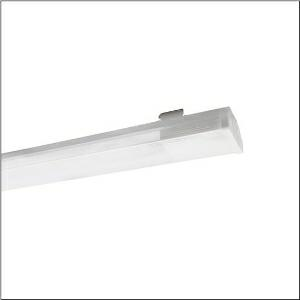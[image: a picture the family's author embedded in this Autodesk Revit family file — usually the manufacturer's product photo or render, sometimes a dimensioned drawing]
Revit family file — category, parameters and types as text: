
# Revit family: modario_31_gen_2_53bm8127u4gxc2_797e
name_source: partatom
category: Lighting Fixtures
units: mm (PartAtom-declared; Revit-internal decimal feet)

## family parameters
Cut with Voids When Loaded = No
Host = Face
Light Source = No
Part Type = Normal
Room Calculation Point = No
Round Connector Dimension = Use Diameter
Shared = No

## types (1)
- Modario 31 Gen.2 (1 x LED, 16360 lm, 90.4 W, 4000K)
    Apparent Load = 90 VA
    CIE Flux Codes = 47 80 95 93 100
    Color Rendering = 80
    Color Temperature = 4000K
    Default Elevation = 1800 mm
    Description = Modario 31 Gen.2, luminaire insert, of sheet steel, coil coated, white, length: 2.392mm, width: 81mm, height: 82mm, 8x system unit, system units: 299mm, LED rated luminous flux: 16.360lm, light colour: 840, SDCM (Standard Deviation of Colour Matching)MacAdam ≤ 3 SDCM (initial), control gear: ON/OFF, with plug, 3-pole, with phase selection, mains connection: 220..240V, AC, 50/60Hz, rated input power: 90W, through-wiring accessed according to module size, primary optical cover: cover, of PMMA, light emission: direct distribution, primary light characteristic: symmetric, protection rating (complete): IP20, protection rating (LED compartment): IP50, insulation class (complete): insulation class I (protective earthing), certification: CE, ENEC, VDE, UKCA, impact resistance: IK03, permissible ambient temperature for indoor applications: -40..+40°C, corresponds to IFS (International Featured Standards) requirements for safety and quality in the food industry, reducing of maximum allowable ambient temperature of 5°C with ceiling mounting, IP40 when using the optional accessory 5TP9018, packaging unit: 1 piece
    Height = 92 mm
    Lamp = 1 x LED
    Lamp Light Flux = 16360 lm
    Lamp Power = 90.4 W
    Lamp count = 1
    Length = 2392 mm
    Luminous efficacy = 181 lm/W
    Manufacturer = Siteco
    ModVariant = No
    Model = 53BM8127U4GXC2
    Mounting Place = Ceiling
    Mounting Type = Pendant
    Number of Poles = 1
    OnlyDefault = Yes
    Power Factor = 1
    Product Name = Modario 31 Gen.2
    Product group = luminaire insert | ceiling pendant
    ProductGroupID = 901
    Protection Class = Protection class I
    Protection Degree = IP 20
    RLX_Detail_Level = 1
    RLX_Emergency_Light_Flux = 0 lm
    RLX_Emergency_Type = 0
    RLX_Emergency_Type_DB = No
    RlxData = <blob elided: 34573 chars, md5=7d11fb18>
    Socket = socket
    Standby Power = 0 W
    System Light Flux = 16360 lm
    System Power = 90 W
    Type Comments = Product without accessories
    Type Image = l_1341883.jpg
    URL = http://relux.com
    VarID = ---
    Voltage = 0 V
    Weight = 0.00 kg
    Width = 81 mm

## geometry (parser evidence)
native form markers: Blend x4, Sweep x11
no freeform markers — native parametric forms only
